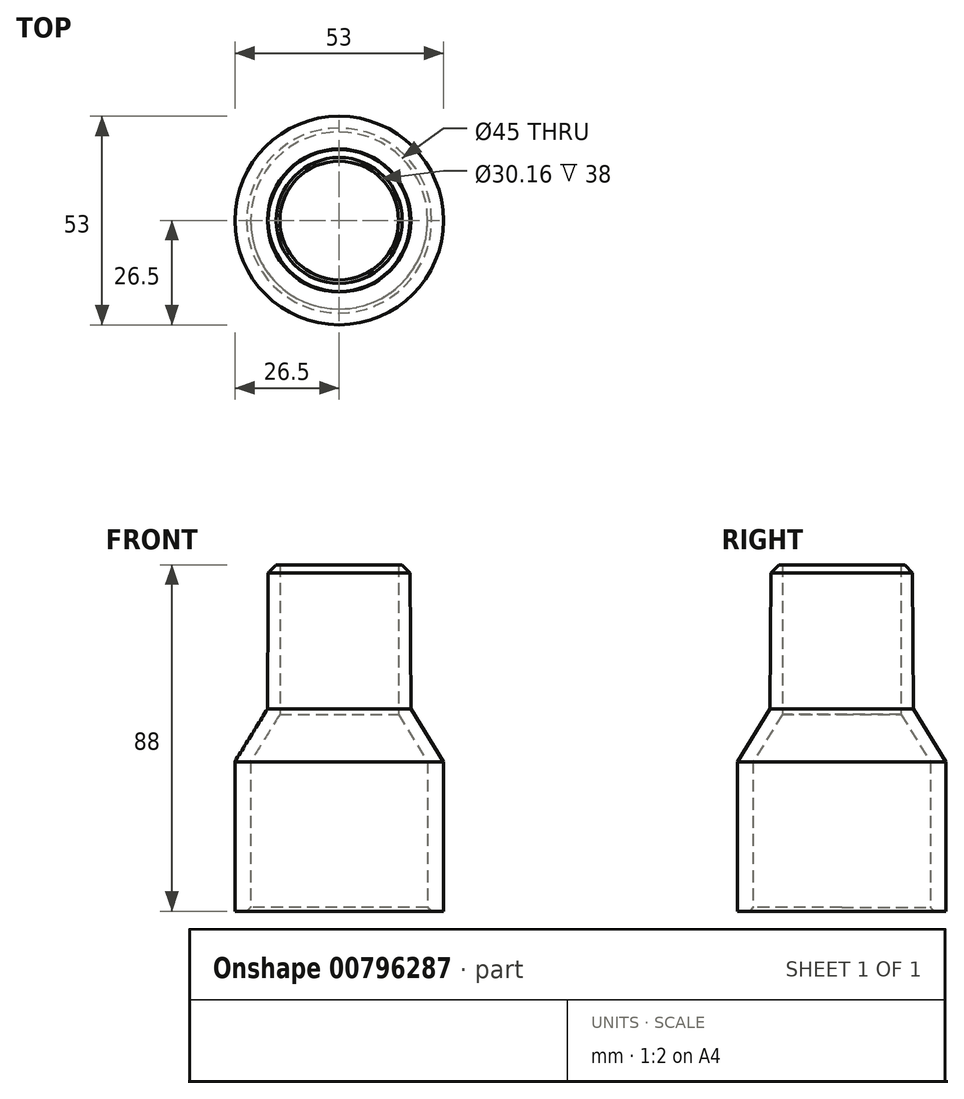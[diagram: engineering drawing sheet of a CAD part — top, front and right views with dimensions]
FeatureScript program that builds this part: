
annotation { "Feature Type Name" : "Feature", "Feature Type Description" : "" }
export const myFeature = defineFeature(function(context is Context, id is Id, definition is map)
    precondition{}
    {
        {
            var Q0;
            Q0=qCreatedBy(makeId("Front.planeOp"),FACE);
            var sketch = newSketch(context, id + "F0", { "sketchPlane" : qUnion([Q0])});
            skLineSegment(sketch, "E0", {"start": v(-41.04, 0) * mm, "end": v(56.48, 0) * mm, "construction": true});
            skLineSegment(sketch, "E1", {"start": v(0, 0) * mm, "end": v(0, 76.78) * mm, "construction": true});
            skLineSegment(sketch, "E2", {"start": v(22.5, 0) * mm, "end": v(22.5, 38) * mm});
            skLineSegment(sketch, "E3", {"start": v(22.5, 38) * mm, "end": v(15.08, 50) * mm});
            skLineSegment(sketch, "E4", {"start": v(15.08, 50) * mm, "end": v(15.08, 88) * mm});
            skLineSegment(sketch, "E5", {"start": v(15.08, 88) * mm, "end": v(18, 88) * mm});
            skLineSegment(sketch, "E6", {"start": v(18, 88) * mm, "end": v(18.2, 51.42) * mm});
            skLineSegment(sketch, "E7", {"start": v(18.2, 51.42) * mm, "end": v(26.5, 38) * mm});
            skLineSegment(sketch, "E8", {"start": v(26.5, 38) * mm, "end": v(26.5, 0) * mm});
            skLineSegment(sketch, "E9", {"start": v(26.5, 0) * mm, "end": v(22.5, 0) * mm});
            skSolve(sketch);
        }
        {
            var Q0;
            Q0=makeQuery(id+"F0.imprint","IMPRINT",FACE,{"disambiguationData":[TD([[makeQuery(id+"F0.imprint","IMPRINT",EDGE,{"derivedFrom":sQuery(id+"F0.wireOp",EDGE,"E2")}),-1.0]])]});
            var Q1;
            Q1=sQuery(id+"F0.wireOp",EDGE,"E1");
            revolve(context, id + "F1", {"surfaceOperationType" : NewSurfaceOperationType.NEW, "entities" : qUnion([Q0]), "axis" : qUnion([Q1]), "revolveType" : RevolveType.FULL});
        }
        {
            var Q0;
            Q0=makeQuery(id+"F1.opRevolve","SWEPT_EDGE",EDGE,{"disambiguationData":[OSD([sQuery(id+"F0.wireOp",EDGE,"E5"),sQuery(id+"F0.wireOp",EDGE,"E6")])]});
            chamfer(context, id + "F2", {"entities" : qUnion([Q0]), "width" : 2 * mm, "tangentPropagation" : true});
        }
        {
            var Q0;
            Q0=makeQuery(id+"F1.opRevolve","SWEPT_EDGE",EDGE,{"disambiguationData":[OSD([sQuery(id+"F0.wireOp",EDGE,"E2"),sQuery(id+"F0.wireOp",EDGE,"E9")])]});
            chamfer(context, id + "F3", {"entities" : qUnion([Q0]), "width" : 1 * mm, "tangentPropagation" : true});
        }
    });
